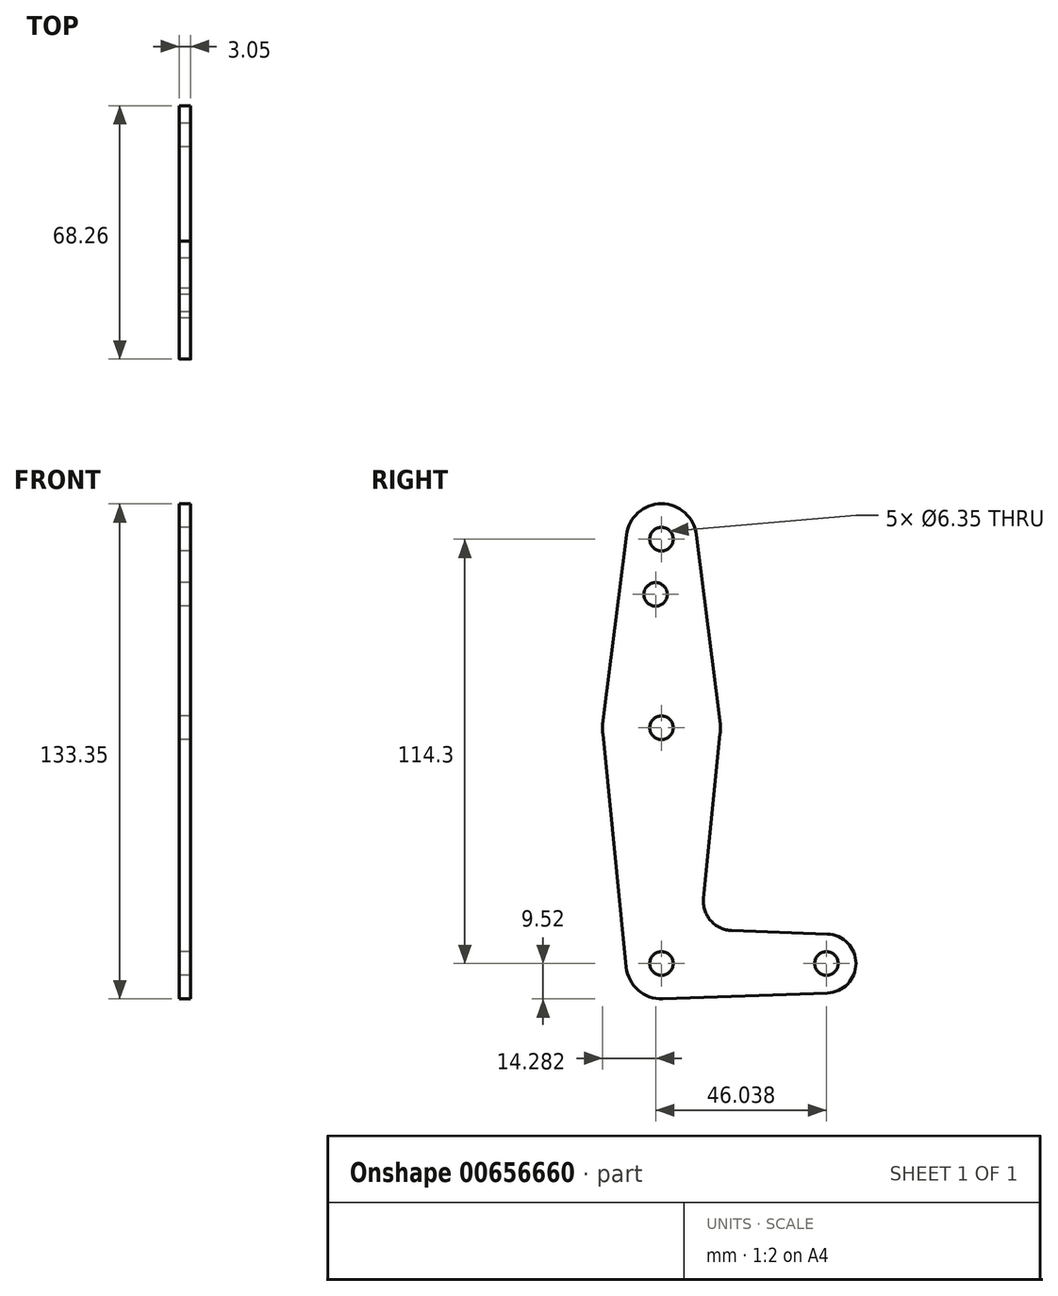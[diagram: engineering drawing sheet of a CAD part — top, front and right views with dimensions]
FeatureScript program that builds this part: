
annotation { "Feature Type Name" : "Feature", "Feature Type Description" : "" }
export const myFeature = defineFeature(function(context is Context, id is Id, definition is map)
    precondition{}
    {
        {
            var Q0;
            Q0=qCreatedBy(makeId("Right.planeOp"),FACE);
            var sketch = newSketch(context, id + "F0", { "sketchPlane" : qUnion([Q0])});
            skLineSegment(sketch, "E0", {"start": v(0, 0) * mm, "end": v(0, 114.3) * mm, "construction": true});
            skLineSegment(sketch, "E1", {"start": v(0, 0) * mm, "end": v(44.45, 0) * mm, "construction": true});
            skCircle(sketch, "E2", {"center": v(44.45, 0) * mm, "radius": 7.94 * mm});
            skCircle(sketch, "E3", {"center": v(0, 0) * mm, "radius": 9.52 * mm});
            skCircle(sketch, "E4", {"center": v(0, 63.5) * mm, "radius": 15.88 * mm});
            skCircle(sketch, "E5", {"center": v(0, 114.3) * mm, "radius": 9.52 * mm});
            skLineSegment(sketch, "E6", {"start": v(44.73, 7.93) * mm, "end": v(18.97, 8.85) * mm});
            skLineSegment(sketch, "E7", {"start": v(44.73, -7.93) * mm, "end": v(0.34, -9.52) * mm});
            skLineSegment(sketch, "E8", {"start": v(11.34, 17.6) * mm, "end": v(15.8, 61.91) * mm});
            skLineSegment(sketch, "E9", {"start": v(15.75, 65.48) * mm, "end": v(9.45, 115.5) * mm});
            skLineSegment(sketch, "E10", {"start": v(-9.45, 115.5) * mm, "end": v(-15.75, 65.48) * mm});
            skLineSegment(sketch, "E11", {"start": v(-15.8, 61.91) * mm, "end": v(-9.48, -0.95) * mm});
            skCircle(sketch, "E12", {"center": v(44.45, 0) * mm, "radius": 3.18 * mm});
            skCircle(sketch, "E13", {"center": v(0, 0) * mm, "radius": 3.18 * mm});
            skCircle(sketch, "E14", {"center": v(0, 63.5) * mm, "radius": 3.18 * mm});
            skCircle(sketch, "E15", {"center": v(0, 114.3) * mm, "radius": 3.18 * mm});
            skCircle(sketch, "E16", {"center": v(-1.59, 99.42) * mm, "radius": 3.18 * mm});
            skArc(sketch, "E17.filletArc", {"start": v(11.34, 17.6) * mm, "mid": v(13.26, 11.57) * mm, "end": v(18.97, 8.85) * mm});
            skSolve(sketch);
        }
        {
            var Q0;
            {var subQ0=sQuery(id+"F0.wireOp",EDGE,"E9");Q0=makeQuery(id+"F0.imprint","IMPRINT",FACE,{"disambiguationData":[TD([[makeQuery(id+"F0.imprint","IMPRINT",EDGE,{"derivedFrom":subQ0}),1.0]])]});}
            var Q1;
            Q1=makeQuery(id+"F0.imprint","IMPRINT",FACE,{"disambiguationData":[TD([[makeQuery(id+"F0.imprint","IMPRINT",EDGE,{"derivedFrom":sQuery(id+"F0.wireOp",EDGE,"E15")}),-1.0]])]});
            var Q2;
            Q2=makeQuery(id+"F0.imprint","IMPRINT",FACE,{"disambiguationData":[TD([[makeQuery(id+"F0.imprint","IMPRINT",EDGE,{"derivedFrom":sQuery(id+"F0.wireOp",EDGE,"E14")}),-1.0]])]});
            var Q3;
            {var subQ5=sQuery(id+"F0.wireOp",EDGE,"E6");Q3=makeQuery(id+"F0.imprint","IMPRINT",FACE,{"disambiguationData":[TD([[makeQuery(id+"F0.imprint","IMPRINT",EDGE,{"derivedFrom":subQ5}),1.0]])]});}
            var Q4;
            Q4=makeQuery(id+"F0.imprint","IMPRINT",FACE,{"disambiguationData":[TD([[makeQuery(id+"F0.imprint","IMPRINT",EDGE,{"derivedFrom":sQuery(id+"F0.wireOp",EDGE,"E13")}),-1.0]])]});
            var Q5;
            Q5=makeQuery(id+"F0.imprint","IMPRINT",FACE,{"disambiguationData":[TD([[makeQuery(id+"F0.imprint","IMPRINT",EDGE,{"derivedFrom":sQuery(id+"F0.wireOp",EDGE,"E12")}),-1.0]])]});
            var Q6;
            Q6=sQuery(id+"F0.wireOp",EDGE,"E11");
            var Q7;
            Q7=sQuery(id+"F0.wireOp",EDGE,"E10");
            var Q8;
            Q8=sQuery(id+"F0.wireOp",EDGE,"E9");
            var Q9;
            Q9=sQuery(id+"F0.wireOp",EDGE,"E8");
            var Q10;
            Q10=sQuery(id+"F0.wireOp",EDGE,"E6");
            var Q11;
            Q11=sQuery(id+"F0.wireOp",EDGE,"E17.filletArc");
            var Q12;
            Q12=sQuery(id+"F0.wireOp",EDGE,"E2");
            var Q13;
            Q13=sQuery(id+"F0.wireOp",EDGE,"E7");
            var Q14;
            Q14=sQuery(id+"F0.wireOp",EDGE,"E3");
            var Q15;
            Q15=sQuery(id+"F0.wireOp",EDGE,"E4");
            var Q16;
            Q16=sQuery(id+"F0.wireOp",EDGE,"E5");
            var Q17;
            Q17=sQuery(id+"F0.wireOp",EDGE,"E15");
            var Q18;
            Q18=sQuery(id+"F0.wireOp",EDGE,"E16");
            var Q19;
            Q19=sQuery(id+"F0.wireOp",EDGE,"E14");
            var Q20;
            Q20=sQuery(id+"F0.wireOp",EDGE,"E13");
            extrude(context, id + "F1", {"entities" : qUnion([Q0, Q1, Q2, Q3, Q4, Q5]), "surfaceEntities" : qUnion([Q6, Q7, Q8, Q9, Q10, Q11, Q12, Q13, Q14, Q15, Q16, Q17, Q18, Q19, Q20]), "depth" : 3.05 * mm, "offsetDistance" : 25.4 * mm});
        }
    });
